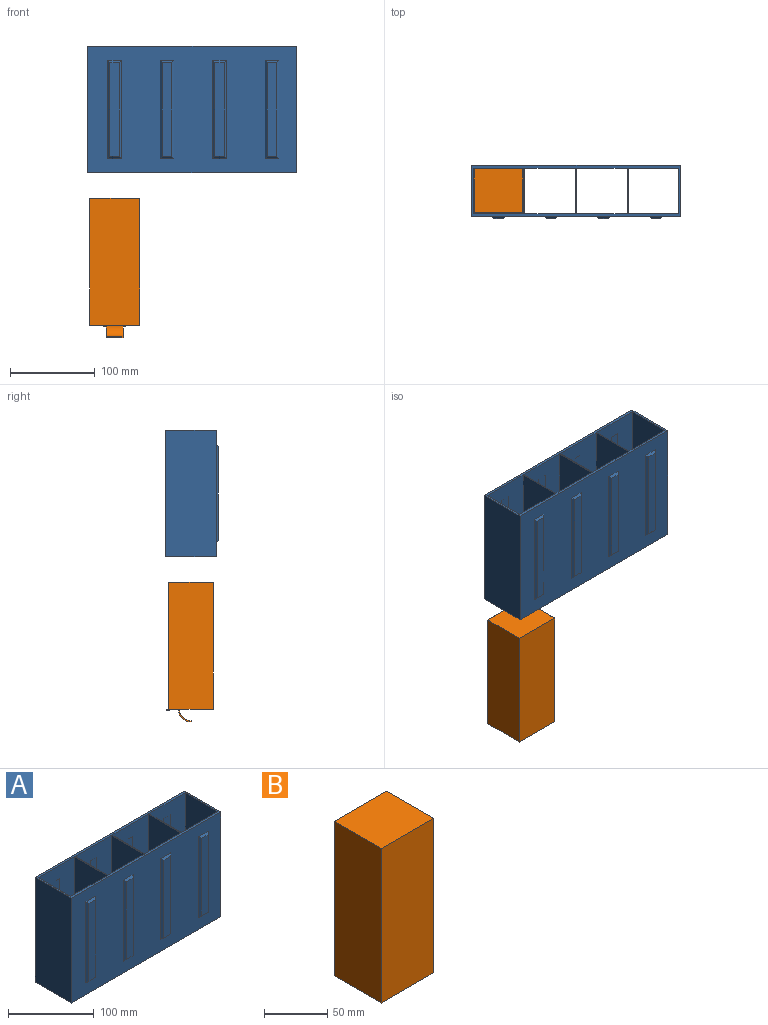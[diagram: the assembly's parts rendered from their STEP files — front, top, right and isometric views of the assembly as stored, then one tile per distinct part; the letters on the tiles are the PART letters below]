
ASSEMBLY  parts=2 mates=1
PART A: 62 faces, bbox 247x62.5x150 mm
  f0: plane 247x150mm, normal (0,1,0), area 29626mm2, adj f1,f2,f3,f5,f26,f27,f28,f29
  f1: plane 247x60mm, normal (0,0,1), area 1860mm2, adj f0,f3,f4,f5,f6,f7,f8,f9
  f2: plane 247x60mm, normal (0,0,-1), area 1860mm2, adj f0,f3,f4,f5,f6,f7,f8,f9
  f3: plane 150x60mm, normal (-1,0,0), area 9000mm2, adj f0,f1,f2,f4
  f4: plane 247x150mm, normal (0,-1,0), area 29626mm2, adj f1,f2,f3,f5,f46,f47,f48,f49
  f5: plane 150x60mm, normal (1,0,0), area 9000mm2, adj f0,f1,f2,f4
  f6: plane 150x60mm, normal (0,-1,0), area 9000mm2, adj f1,f2,f7,f9
  f7: plane 150x54mm, normal (1,0,0), area 8100mm2, adj f1,f2,f6,f8
  f8: plane 150x60mm, normal (0,1,0), area 9000mm2, adj f1,f2,f7,f9
  f9: plane 150x54mm, normal (-1,0,0), area 8100mm2, adj f1,f2,f6,f8
  f10: plane 150x60mm, normal (0,-1,0), area 9000mm2, adj f1,f2,f11,f13
  f11: plane 150x54mm, normal (1,0,0), area 8100mm2, adj f1,f2,f10,f12
  f12: plane 150x60mm, normal (0,1,0), area 9000mm2, adj f1,f2,f11,f13
  f13: plane 150x54mm, normal (-1,0,0), area 8100mm2, adj f1,f2,f10,f12
  f14: plane 150x60mm, normal (0,-1,0), area 9000mm2, adj f1,f2,f15,f17
  f15: plane 150x54mm, normal (1,0,0), area 8100mm2, adj f1,f2,f14,f16
  f16: plane 150x60mm, normal (0,1,0), area 9000mm2, adj f1,f2,f15,f17
  f17: plane 150x54mm, normal (-1,0,0), area 8100mm2, adj f1,f2,f14,f16
  f18: plane 150x60mm, normal (0,-1,0), area 9000mm2, adj f1,f2,f19,f21
  f19: plane 150x54mm, normal (1,0,0), area 8100mm2, adj f1,f2,f18,f20
  f20: plane 150x60mm, normal (0,1,0), area 9000mm2, adj f1,f2,f19,f21
  f21: plane 150x54mm, normal (-1,0,0), area 8100mm2, adj f1,f2,f18,f20
  f22: plane 111x11mm, normal (0,1,0), area 1221mm2, adj f38,f39,f40,f41
  f23: plane 111x11mm, normal (0,1,0), area 1221mm2, adj f30,f31,f32,f33
  f24: plane 111x11mm, normal (0,1,0), area 1221mm2, adj f26,f27,f28,f29
  f25: plane 111x11mm, normal (0,1,0), area 1221mm2, adj f34,f35,f36,f37
  f26: plane 16x2.5mm, normal (0,0.71,0.71), area 47.7mm2, adj f0,f24,f27,f28
  f27: plane 116x2.5mm, normal (0.71,0.71,0), area 401.3mm2, adj f0,f24,f26,f29
  f28: plane 116x2.5mm, normal (-0.71,0.71,0), area 401.3mm2, adj f0,f24,f26,f29
  f29: plane 16x2.5mm, normal (0,0.71,-0.71), area 47.7mm2, adj f0,f24,f27,f28
  f30: plane 16x2.5mm, normal (0,0.71,0.71), area 47.7mm2, adj f0,f23,f31,f32
  f31: plane 116x2.5mm, normal (0.71,0.71,0), area 401.3mm2, adj f0,f23,f30,f33
  f32: plane 116x2.5mm, normal (-0.71,0.71,0), area 401.3mm2, adj f0,f23,f30,f33
  f33: plane 16x2.5mm, normal (0,0.71,-0.71), area 47.7mm2, adj f0,f23,f31,f32
  f34: plane 16x2.5mm, normal (0,0.71,-0.71), area 47.7mm2, adj f0,f25,f35,f36
  f35: plane 116x2.5mm, normal (0.71,0.71,0), area 401.3mm2, adj f0,f25,f34,f37
  f36: plane 116x2.5mm, normal (-0.71,0.71,0), area 401.3mm2, adj f0,f25,f34,f37
  f37: plane 16x2.5mm, normal (0,0.71,0.71), area 47.7mm2, adj f0,f25,f35,f36
  f38: plane 16x2.5mm, normal (0,0.71,0.71), area 47.7mm2, adj f0,f22,f39,f40
  f39: plane 116x2.5mm, normal (0.71,0.71,0), area 401.3mm2, adj f0,f22,f38,f41
  f40: plane 116x2.5mm, normal (-0.71,0.71,0), area 401.3mm2, adj f0,f22,f38,f41
  f41: plane 16x2.5mm, normal (0,0.71,-0.71), area 47.7mm2, adj f0,f22,f39,f40
  f42: plane 111x11mm, normal (0,-1,0), area 1221mm2, adj f58,f59,f60,f61
  f43: plane 111x11mm, normal (0,-1,0), area 1221mm2, adj f54,f55,f56,f57
  f44: plane 111x11mm, normal (0,-1,0), area 1221mm2, adj f50,f51,f52,f53
  f45: plane 111x11mm, normal (0,-1,0), area 1221mm2, adj f46,f47,f48,f49
  f46: plane 116x2.5mm, normal (-0.71,-0.71,0), area 401.3mm2, adj f4,f45,f47,f48
  f47: plane 16x2.5mm, normal (0,-0.71,0.71), area 47.7mm2, adj f4,f45,f46,f49
  f48: plane 16x2.5mm, normal (0,-0.71,-0.71), area 47.7mm2, adj f4,f45,f46,f49
  f49: plane 116x2.5mm, normal (0.71,-0.71,0), area 401.3mm2, adj f4,f45,f47,f48
  f50: plane 116x2.5mm, normal (-0.71,-0.71,0), area 401.3mm2, adj f4,f44,f51,f52
  f51: plane 16x2.5mm, normal (0,-0.71,0.71), area 47.7mm2, adj f4,f44,f50,f53
  f52: plane 16x2.5mm, normal (0,-0.71,-0.71), area 47.7mm2, adj f4,f44,f50,f53
  f53: plane 116x2.5mm, normal (0.71,-0.71,0), area 401.3mm2, adj f4,f44,f51,f52
  f54: plane 16x2.5mm, normal (0,-0.71,-0.71), area 47.7mm2, adj f4,f43,f55,f56
  f55: plane 116x2.5mm, normal (-0.71,-0.71,0), area 401.3mm2, adj f4,f43,f54,f57
  f56: plane 116x2.5mm, normal (0.71,-0.71,0), area 401.3mm2, adj f4,f43,f54,f57
  f57: plane 16x2.5mm, normal (0,-0.71,0.71), area 47.7mm2, adj f4,f43,f55,f56
  f58: plane 116x2.5mm, normal (-0.71,-0.71,0), area 401.3mm2, adj f4,f42,f59,f60
  f59: plane 16x2.5mm, normal (0,-0.71,0.71), area 47.7mm2, adj f4,f42,f58,f61
  f60: plane 16x2.5mm, normal (0,-0.71,-0.71), area 47.7mm2, adj f4,f42,f58,f61
  f61: plane 116x2.5mm, normal (0.71,-0.71,0), area 401.3mm2, adj f4,f42,f59,f60
PART B: 22 faces, bbox 59x56x165 mm
  f0: plane 59x53mm, normal (0,0,-1), area 3007mm2, adj f1,f2,f3,f4,f14,f15,f16,f17
  f1: plane 150x59mm, normal (0,1,0), area 414mm2, adj f0,f2,f4,f5,f6,f8,f9,f10
  f2: plane 150x53mm, normal (-1,0,0), area 7950mm2, adj f0,f1,f3,f5
  f3: plane 150x59mm, normal (0,-1,0), area 8850mm2, adj f0,f2,f4,f5
  f4: plane 150x53mm, normal (1,0,0), area 7950mm2, adj f0,f1,f3,f5
  f5: plane 59x53mm, normal (0,0,1), area 3127mm2, adj f1,f2,f3,f4
  f6: plane 148x52mm, normal (1,0,0), area 7696mm2, adj f1,f7,f9,f10
  f7: plane 148x57mm, normal (0,1,0), area 8436mm2, adj f6,f8,f9,f10
  f8: plane 148x52mm, normal (-1,0,0), area 7696mm2, adj f1,f7,f9,f10
  f9: plane 57x52mm, normal (0,0,-1), area 2964mm2, adj f1,f6,f7,f8
  f10: plane 57x52mm, normal (0,0,1), area 2964mm2, adj f1,f6,f7,f8
  f11: plane 30x3mm, normal (0,0,1), area 90mm2, adj f1,f12,f14,f16
  f12: plane 30x1mm, normal (0,1,0), area 28.3mm2, adj f11,f13,f14,f16
  f13: plane 26.54x4.27mm, normal (0,0,-1), area 113.3mm2, adj f12,f14,f15,f16
  f14: plane 6x1.73mm, normal (0.5,0,-0.87), area 10.3mm2, adj f0,f11,f12,f13,f15
  f15: plane 30x1.73mm, normal (0,-0.5,-0.87), area 56.5mm2, adj f0,f13,f14,f16
  f16: plane 6x1.73mm, normal (-0.5,0,-0.87), area 10.3mm2, adj f0,f11,f12,f13,f15
  f17: cylinder r=15mm len=20mm, axis (-1,0,0), area 471.2mm2, adj f0,f18,f20,f21
  f18: plane 20x1.5mm, normal (0,-1,0), area 30mm2, adj f17,f19,f20,f21
  f19: cylinder r=13.5mm len=20mm, axis (-1,0,0), area 424.1mm2, adj f0,f18,f20,f21
  f20: plane 15x15mm, normal (1,0,0), area 33.6mm2, adj f0,f17,f18,f19
  f21: plane 15x15mm, normal (-1,0,0), area 33.6mm2, adj f0,f17,f18,f19
PLACE A rot(axis=(-0.11,-0.99,0.1),0deg) t=(-93.3,11.64,77.15)mm fixed
PLACE B t=(-78.3,-83.95,-102.85)mm
MATE slider B.f0 <-> A.f2  axis (0,0,-1) through (-191.24,-39.76,-102.85)mm
